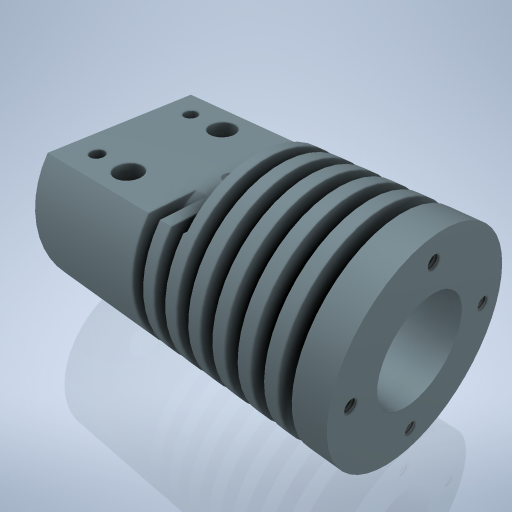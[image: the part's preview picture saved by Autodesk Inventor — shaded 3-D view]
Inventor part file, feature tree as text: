
AUTODESK INVENTOR PART (.ipt)
format: ipt  version: 2024.2 (Build 282272000, 272)  size: 455,680 bytes
history: native  units: mm
features: sketch x11, hole x8, revolve x2, plane x2, extrude x1, projected_geometry x1
ambient origin geometry x8: Origin, YZ Plane, XZ Plane, XY Plane, X Axis, Y Axis, Z Axis, Center Point
bodies: Volumenkörper1 (feature_tree)
feature tree (25):
  revolve  "Umdrehung1"
  hole  "Bohrung1"  [1 undecoded]
  hole  "Bohrung2"  [1 undecoded]
  hole  "Bohrung3"  [1 undecoded]
  plane  "Arbeitsebene1"
  revolve  "Umdrehung2"
  extrude  "Extrusion1"  Depth=2.5mm
  hole  "Bohrung4"  [1 undecoded]
  hole  "Bohrung5"  [1 undecoded]
  hole  "Bohrung6"  [1 undecoded]
  hole  "Bohrung7"  [1 undecoded]
  plane  "Arbeitsebene2"
  hole  "Bohrung8"  [1 undecoded]
  sketch  "Skizze3"  dims[d8=64.0mm d9=64.0mm]
  sketch  "Skizze4"  dims[d10=32.5mm d11=6.0mm]
  sketch  "Skizze5"  dims[d12=2.5mm d13=2.5mm]
  sketch  "Skizze6"  dims[d14=2.5mm d15=2.5mm]
  sketch  "Skizze7"  dims[d16=2.5mm d17=2.5mm]
  projected_geometry  "Projizierte Kontur1"
  sketch  "Skizze8"  dims[d18=2.5mm d19=2.5mm]
  sketch  "Skizze9"  dims[d20=2.5mm d22=2.5mm]
  sketch  "Skizze10"  dims[d23=2.5mm d24=27.0mm]
  sketch  "Skizze11"  dims[d25=39.0mm d26=90.0deg]
  sketch  "Skizze12"  dims[d27=8.0mm d28=6.0mm d29=4.0mm d30=2.0mm d31=90.0deg d32=24.435mm d33=0.0mm]
  sketch  "Skizze14"  dims[d34=10.0mm d35=6.0mm d36=4.0mm d37=2.0mm d38=90.0deg d39=8.0mm d40=0.0mm d41=12.0mm d42=6.0mm d43=4.0mm d44=2.0mm d45=90.0deg d46=6.0mm d47=0.0mm d48=0.0mm d51=45.5mm d52=90.0deg d53=19.0mm d54=16.88mm d55=12.0mm d56=33.5mm d57=0.0mm d58=5.5mm d59=6.0mm d60=4.0mm d61=2.0mm d62=90.0deg d63=6.0mm d64=0.0mm d65=14.0mm d66=20.0mm d67=3.0mm d68=6.0mm d69=4.0mm d70=2.0mm d71=90.0deg d72=8.0mm d73=0.0mm d74=20.0mm d75=6.0mm d76=3.0mm d77=6.0mm d78=4.0mm d79=2.0mm d80=90.0deg d81=19.5mm d82=0.0mm d83=26.5mm d84=30.0mm d85=2.459mm d86=6.0mm d87=4.0mm d88=2.0mm d89=90.0deg d90=6.0mm d91=0.0mm d92=-19.5mm d93=14.0mm d94=5.5mm d95=6.0mm d96=10.0mm d97=14.0mm d98=90.0deg d99=17.5mm d100=0.0mm]
note: 8 required parameter values undecoded (feature->parameter linkage not recoverable at this tier; creation-order binding heuristic only, values carry confidence <= 0.55)
